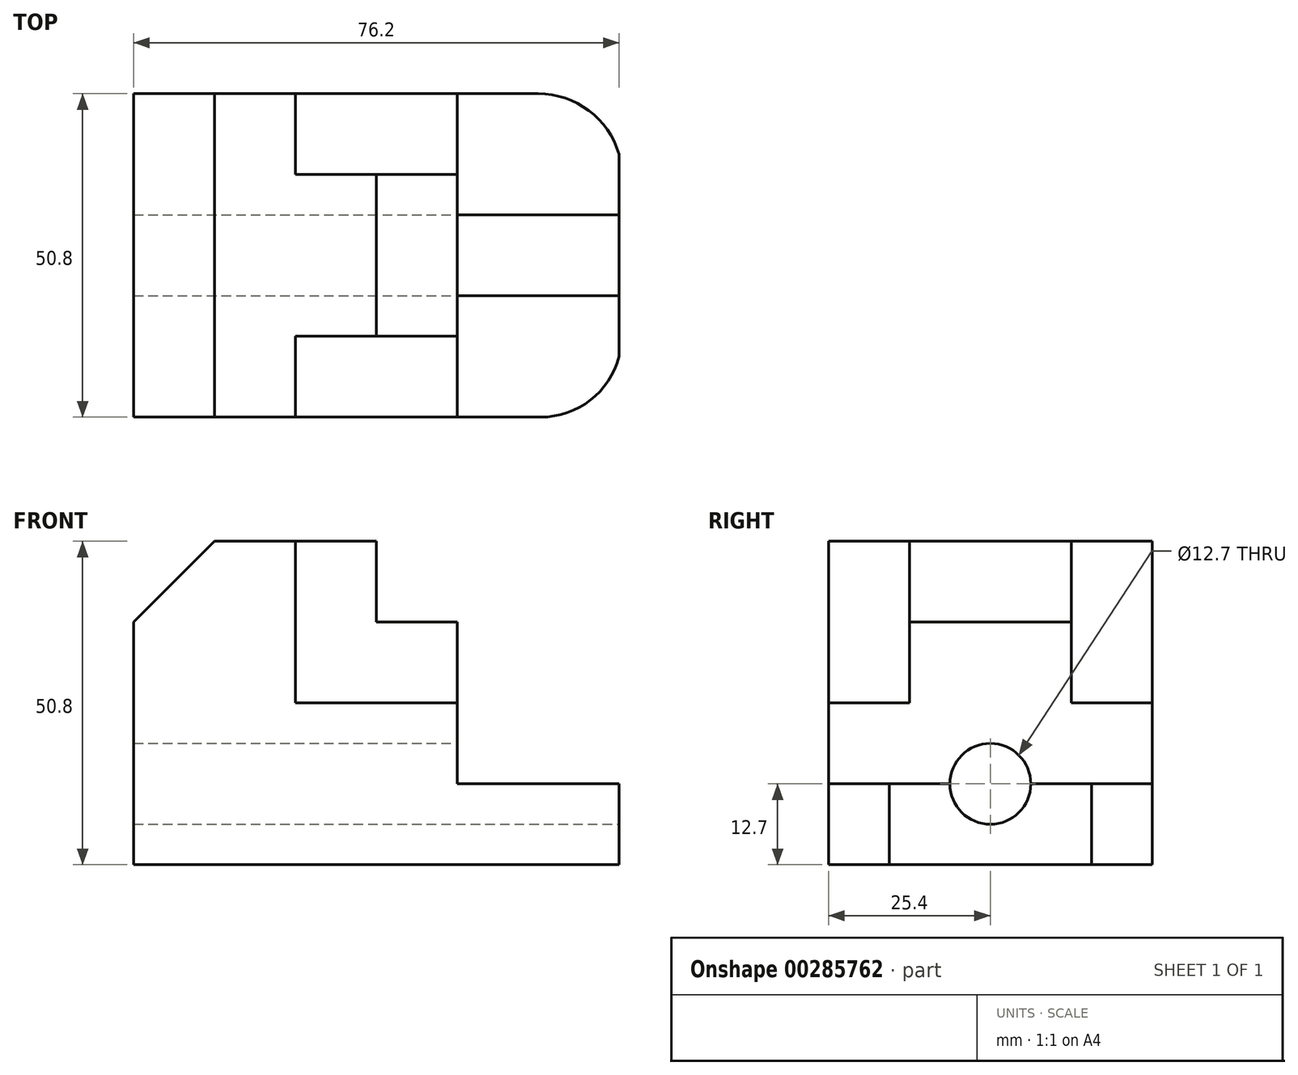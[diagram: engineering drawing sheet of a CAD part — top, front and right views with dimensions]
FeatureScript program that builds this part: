
annotation { "Feature Type Name" : "Feature", "Feature Type Description" : "" }
export const myFeature = defineFeature(function(context is Context, id is Id, definition is map)
    precondition{}
    {
        {
            var Q0;
            Q0=qCreatedBy(makeId("Front.planeOp"),FACE);
            var sketch = newSketch(context, id + "F0", { "sketchPlane" : qUnion([Q0])});
            skLineSegment(sketch, "E0", {"start": v(0, 0) * mm, "end": v(0, 38.1) * mm});
            skLineSegment(sketch, "E1", {"start": v(0, 38.1) * mm, "end": v(12.7, 50.8) * mm});
            skLineSegment(sketch, "E2", {"start": v(12.7, 50.8) * mm, "end": v(25.4, 50.8) * mm});
            skLineSegment(sketch, "E3", {"start": v(25.4, 50.8) * mm, "end": v(25.4, 25.4) * mm});
            skLineSegment(sketch, "E4", {"start": v(25.4, 25.4) * mm, "end": v(50.8, 25.4) * mm});
            skLineSegment(sketch, "E5", {"start": v(50.8, 25.4) * mm, "end": v(50.8, 12.7) * mm});
            skLineSegment(sketch, "E6", {"start": v(50.8, 12.7) * mm, "end": v(76.2, 12.7) * mm});
            skLineSegment(sketch, "E7", {"start": v(76.2, 12.7) * mm, "end": v(76.2, 0) * mm});
            skLineSegment(sketch, "E8", {"start": v(76.2, 0) * mm, "end": v(0, 0) * mm});
            skSolve(sketch);
        }
        {
            var Q0;
            Q0 = qSketchRegion(id + "F0", true);
            extrude(context, id + "F1", {"entities" : qUnion([Q0]), "oppositeDirection" : true, "depth" : 25.4 * mm, "hasSecondDirection" : true, "secondDirectionOppositeDirection" : false, "secondDirectionDepth" : 25.4 * mm});
        }
        {
            var Q0;
            Q0=makeQuery(id+"F1.opExtrude","SWEPT_FACE",FACE,{"disambiguationData":[OSD([sQuery(id+"F0.wireOp",EDGE,"E3")])]});
            var sketch = newSketch(context, id + "F2", { "sketchPlane" : qUnion([Q0])});
            skLineSegment(sketch, "E9.bottom", {"start": v(-12.7, 50.8) * mm, "end": v(12.7, 50.8) * mm});
            skLineSegment(sketch, "E9.top", {"start": v(-12.7, 38.1) * mm, "end": v(12.7, 38.1) * mm});
            skLineSegment(sketch, "E9.left", {"start": v(-12.7, 50.8) * mm, "end": v(-12.7, 38.1) * mm});
            skLineSegment(sketch, "E9.right", {"start": v(12.7, 50.8) * mm, "end": v(12.7, 38.1) * mm});
            skSolve(sketch);
        }
        {
            var Q0;
            Q0 = qSketchRegion(id + "F2", true);
            extrude(context, id + "F3", {"entities" : qUnion([Q0]), "operationType" : NewBodyOperationType.ADD, "depth" : 12.7 * mm});
        }
        {
            var Q0;
            Q0=makeQuery(id+"F1.opExtrude","SWEPT_FACE",FACE,{"disambiguationData":[OSD([sQuery(id+"F0.wireOp",EDGE,"E3")])]});
            var sketch = newSketch(context, id + "F4", { "sketchPlane" : qUnion([Q0])});
            skLineSegment(sketch, "E10.bottom", {"start": v(-25.4, 25.4) * mm, "end": v(25.4, 25.4) * mm});
            skLineSegment(sketch, "E10.top", {"start": v(-25.4, 38.1) * mm, "end": v(25.4, 38.1) * mm});
            skLineSegment(sketch, "E10.left", {"start": v(-25.4, 25.4) * mm, "end": v(-25.4, 38.1) * mm});
            skLineSegment(sketch, "E10.right", {"start": v(25.4, 25.4) * mm, "end": v(25.4, 38.1) * mm});
            skSolve(sketch);
        }
        {
            var Q0;
            Q0 = qSketchRegion(id + "F4", true);
            extrude(context, id + "F5", {"entities" : qUnion([Q0]), "operationType" : NewBodyOperationType.ADD, "depth" : 25.4 * mm});
        }
        {
            var Q0;
            Q0=makeQuery(id+"F5.boolean.opBoolean","MERGE",FACE,{"derivedFrom":[makeQuery(id+"F1.opExtrude","CAP_FACE",FACE,{"disambiguationData":[OSD([sQuery(id+"F0.wireOp",EDGE,"E0"),sQuery(id+"F0.wireOp",EDGE,"E1"),sQuery(id+"F0.wireOp",EDGE,"E2"),sQuery(id+"F0.wireOp",EDGE,"E3"),sQuery(id+"F0.wireOp",EDGE,"E4"),sQuery(id+"F0.wireOp",EDGE,"E5"),sQuery(id+"F0.wireOp",EDGE,"E6"),sQuery(id+"F0.wireOp",EDGE,"E7"),sQuery(id+"F0.wireOp",EDGE,"E8")])],"isStart":true}),makeQuery(id+"F5.opExtrude","SWEPT_FACE",FACE,{"disambiguationData":[OSD([sQuery(id+"F4.wireOp",EDGE,"E10.left")])]})]});
            var sketch = newSketch(context, id + "F6", { "sketchPlane" : qUnion([Q0])});
            skLineSegment(sketch, "E11.bottom", {"start": v(25.4, 38.1) * mm, "end": v(50.8, 38.1) * mm});
            skLineSegment(sketch, "E11.top", {"start": v(25.4, 25.4) * mm, "end": v(50.8, 25.4) * mm});
            skLineSegment(sketch, "E11.left", {"start": v(25.4, 38.1) * mm, "end": v(25.4, 25.4) * mm});
            skLineSegment(sketch, "E11.right", {"start": v(50.8, 38.1) * mm, "end": v(50.8, 25.4) * mm});
            skSolve(sketch);
        }
        {
            var Q0;
            Q0 = qSketchRegion(id + "F6", true);
            extrude(context, id + "F7", {"entities" : qUnion([Q0]), "operationType" : NewBodyOperationType.REMOVE, "oppositeDirection" : true, "depth" : 12.7 * mm});
        }
        {
            var Q0;
            Q0=makeQuery(id+"F5.boolean.opBoolean","MERGE",FACE,{"derivedFrom":[makeQuery(id+"F1.opExtrude","CAP_FACE",FACE,{"disambiguationData":[OSD([sQuery(id+"F0.wireOp",EDGE,"E0"),sQuery(id+"F0.wireOp",EDGE,"E1"),sQuery(id+"F0.wireOp",EDGE,"E2"),sQuery(id+"F0.wireOp",EDGE,"E3"),sQuery(id+"F0.wireOp",EDGE,"E4"),sQuery(id+"F0.wireOp",EDGE,"E5"),sQuery(id+"F0.wireOp",EDGE,"E6"),sQuery(id+"F0.wireOp",EDGE,"E7"),sQuery(id+"F0.wireOp",EDGE,"E8")])],"isStart":false}),makeQuery(id+"F5.opExtrude","SWEPT_FACE",FACE,{"disambiguationData":[OSD([sQuery(id+"F4.wireOp",EDGE,"E10.right")])]})]});
            var sketch = newSketch(context, id + "F8", { "sketchPlane" : qUnion([Q0])});
            skLineSegment(sketch, "E12.bottom", {"start": v(-50.8, 38.1) * mm, "end": v(-25.4, 38.1) * mm});
            skLineSegment(sketch, "E12.top", {"start": v(-50.8, 25.4) * mm, "end": v(-25.4, 25.4) * mm});
            skLineSegment(sketch, "E12.left", {"start": v(-50.8, 38.1) * mm, "end": v(-50.8, 25.4) * mm});
            skLineSegment(sketch, "E12.right", {"start": v(-25.4, 38.1) * mm, "end": v(-25.4, 25.4) * mm});
            skSolve(sketch);
        }
        {
            var Q0;
            Q0 = qSketchRegion(id + "F8", true);
            extrude(context, id + "F9", {"entities" : qUnion([Q0]), "operationType" : NewBodyOperationType.REMOVE, "oppositeDirection" : true, "depth" : 12.7 * mm});
        }
        {
            var Q0;
            Q0=makeQuery(id+"F1.opExtrude","SWEPT_FACE",FACE,{"disambiguationData":[OSD([sQuery(id+"F0.wireOp",EDGE,"E7")])]});
            var sketch = newSketch(context, id + "F10", { "sketchPlane" : qUnion([Q0])});
            skCircle(sketch, "E13", {"center": v(0, 12.7) * mm, "radius": 6.35 * mm});
            skSolve(sketch);
        }
        {
            var Q0;
            Q0 = qSketchRegion(id + "F10", true);
            extrude(context, id + "F11", {"entities" : qUnion([Q0]), "operationType" : NewBodyOperationType.REMOVE, "endBound" : BoundingType.THROUGH_ALL, "oppositeDirection" : true, "depth" : 25.4 * mm});
        }
        {
            var Q0;
            {var subQ0=sQuery(id+"F4.wireOp",EDGE,"E10.left");var subQ3=sQuery(id+"F0.wireOp",EDGE,"E6");Q0=makeQuery(id+"F11.boolean.opBoolean","SPLIT",FACE,{"disambiguationData":[TD([makeQuery(id+"F5.opExtrude","SWEPT_FACE",FACE,{"disambiguationData":[OSD([subQ0])]})])],"derivedFrom":makeQuery(id+"F1.opExtrude","SWEPT_FACE",FACE,{"disambiguationData":[OSD([subQ3])]})});}
            var sketch = newSketch(context, id + "F12", { "sketchPlane" : qUnion([Q0])});
            skLineSegment(sketch, "E14", {"start": v(76.2, -15.87) * mm, "end": v(76.2, -25.4) * mm});
            skLineSegment(sketch, "E15", {"start": v(76.2, -25.4) * mm, "end": v(63.9, -25.4) * mm});
            skArc(sketch, "E16", {"start": v(63.9, -25.4) * mm, "mid": v(71.68, -22.74) * mm, "end": v(76.2, -15.87) * mm});
            skSolve(sketch);
        }
        {
            var Q0;
            Q0 = qSketchRegion(id + "F12", true);
            extrude(context, id + "F13", {"entities" : qUnion([Q0]), "operationType" : NewBodyOperationType.REMOVE, "endBound" : BoundingType.THROUGH_ALL, "oppositeDirection" : true, "depth" : 25.4 * mm});
        }
        {
            var Q0;
            {var subQ0=sQuery(id+"F4.wireOp",EDGE,"E10.right");var subQ3=sQuery(id+"F0.wireOp",EDGE,"E6");Q0=makeQuery(id+"F11.boolean.opBoolean","SPLIT",FACE,{"disambiguationData":[TD([makeQuery(id+"F5.opExtrude","SWEPT_FACE",FACE,{"disambiguationData":[OSD([subQ0])]})])],"derivedFrom":makeQuery(id+"F1.opExtrude","SWEPT_FACE",FACE,{"disambiguationData":[OSD([subQ3])]})});}
            var sketch = newSketch(context, id + "F14", { "sketchPlane" : qUnion([Q0])});
            skLineSegment(sketch, "E17", {"start": v(76.2, 15.88) * mm, "end": v(76.2, 25.4) * mm});
            skLineSegment(sketch, "E18", {"start": v(76.2, 25.4) * mm, "end": v(63.5, 25.4) * mm});
            skArc(sketch, "E19", {"start": v(76.2, 15.88) * mm, "mid": v(71.44, 22.75) * mm, "end": v(63.5, 25.4) * mm});
            skSolve(sketch);
        }
        {
            var Q0;
            Q0 = qSketchRegion(id + "F14", true);
            extrude(context, id + "F15", {"entities" : qUnion([Q0]), "operationType" : NewBodyOperationType.REMOVE, "endBound" : BoundingType.THROUGH_ALL, "oppositeDirection" : true, "depth" : 25.4 * mm});
        }
    });
